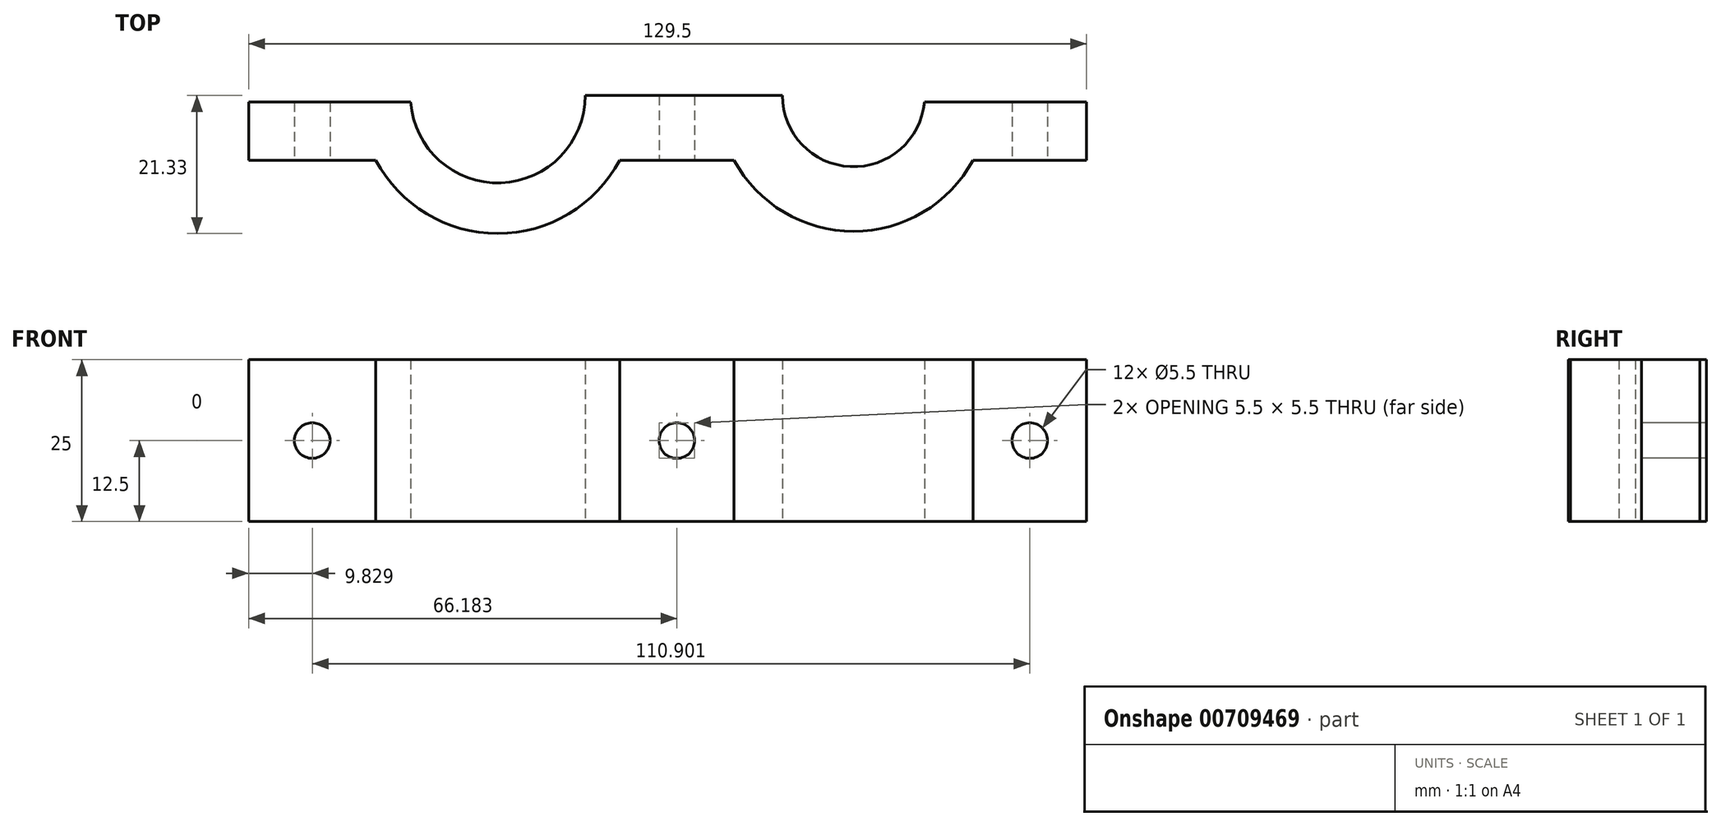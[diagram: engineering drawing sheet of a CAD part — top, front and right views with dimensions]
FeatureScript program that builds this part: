
annotation { "Feature Type Name" : "Feature", "Feature Type Description" : "" }
export const myFeature = defineFeature(function(context is Context, id is Id, definition is map)
    precondition{}
    {
        {
            var Q0;
            Q0=qCreatedBy(makeId("Top.planeOp"),FACE);
            var sketch = newSketch(context, id + "F0", { "sketchPlane" : qUnion([Q0])});
            skLineSegment(sketch, "E0", {"start": v(-63.41, -1.47) * mm, "end": v(-38.41, -1.47) * mm});
            skLineSegment(sketch, "E1", {"start": v(-11.41, -1.47) * mm, "end": v(19.09, -1.47) * mm});
            skLineSegment(sketch, "E2", {"start": v(41.09, -1.47) * mm, "end": v(66.09, -1.47) * mm});
            skLineSegment(sketch, "E3", {"start": v(66.09, -1.47) * mm, "end": v(66.09, -11.47) * mm});
            skLineSegment(sketch, "E4", {"start": v(66.09, -11.47) * mm, "end": v(48.55, -11.47) * mm});
            skLineSegment(sketch, "E5", {"start": v(-63.41, -1.47) * mm, "end": v(-63.41, -11.47) * mm});
            skLineSegment(sketch, "E6", {"start": v(-63.41, -11.47) * mm, "end": v(-43.75, -11.47) * mm});
            skArc(sketch, "E7", {"start": v(-38.41, -1.47) * mm, "mid": v(-24.91, -14.97) * mm, "end": v(-11.41, -1.47) * mm});
            skArc(sketch, "E8", {"start": v(19.09, -1.47) * mm, "mid": v(30.09, -12.47) * mm, "end": v(41.09, -1.47) * mm});
            skLineSegment(sketch, "E9", {"start": v(-6.08, -11.47) * mm, "end": v(11.62, -11.47) * mm});
            skArc(sketch, "E10", {"start": v(-43.75, -11.47) * mm, "mid": v(-24.91, -22.8) * mm, "end": v(-6.08, -11.47) * mm});
            skArc(sketch, "E11", {"start": v(11.62, -11.47) * mm, "mid": v(30.09, -22.47) * mm, "end": v(48.55, -11.47) * mm});
            skLineSegment(sketch, "E12", {"start": v(-24.91, -14.97) * mm, "end": v(-24.91, -22.8) * mm, "construction": true});
            skLineSegment(sketch, "E13", {"start": v(30.09, -12.47) * mm, "end": v(30.09, -22.47) * mm, "construction": true});
            skLineSegment(sketch, "E14", {"start": v(3.84, -1.47) * mm, "end": v(3.84, -11.47) * mm, "construction": true});
            skLineSegment(sketch, "E15", {"start": v(41.09, -1.47) * mm, "end": v(19.09, -1.47) * mm, "construction": true});
            skLineSegment(sketch, "E16", {"start": v(-11.41, -1.47) * mm, "end": v(-38.41, -1.47) * mm, "construction": true});
            skSolve(sketch);
        }
        {
            var Q0;
            Q0=makeQuery(id+"F0.imprint","IMPRINT",FACE,{"disambiguationData":[TD([[makeQuery(id+"F0.imprint","IMPRINT",EDGE,{"derivedFrom":sQuery(id+"F0.wireOp",EDGE,"E0")}),-1.0]])]});
            extrude(context, id + "F1", {"entities" : qUnion([Q0]), "depth" : 25 * mm, "offsetDistance" : 25 * mm});
        }
        {
            var Q0;
            Q0=makeQuery(id+"F1.opExtrude","SWEPT_FACE",FACE,{"disambiguationData":[OSD([sQuery(id+"F0.wireOp",EDGE,"E6")])]});
            var sketch = newSketch(context, id + "F2", { "sketchPlane" : qUnion([Q0])});
            skLineSegment(sketch, "E17", {"start": v(-53.58, 0) * mm, "end": v(-53.58, 25) * mm, "construction": true});
            skPoint(sketch, "E18", {"position": v(-53.58, 12.5) * mm});
            skSolve(sketch);
        }
        {
            var Q0;
            Q0=makeQuery(id+"F1.opExtrude","SWEPT_FACE",FACE,{"disambiguationData":[OSD([sQuery(id+"F0.wireOp",EDGE,"E4")])]});
            var sketch = newSketch(context, id + "F3", { "sketchPlane" : qUnion([Q0])});
            skLineSegment(sketch, "E19", {"start": v(57.32, 25) * mm, "end": v(57.32, 0) * mm, "construction": true});
            skPoint(sketch, "E20", {"position": v(57.32, 12.5) * mm});
            skSolve(sketch);
        }
        {
            var Q0;
            Q0=makeQuery(id+"F1.opExtrude","SWEPT_FACE",FACE,{"disambiguationData":[OSD([sQuery(id+"F0.wireOp",EDGE,"E9")])]});
            var sketch = newSketch(context, id + "F4", { "sketchPlane" : qUnion([Q0])});
            skLineSegment(sketch, "E21", {"start": v(2.77, 25) * mm, "end": v(2.77, 0) * mm, "construction": true});
            skPoint(sketch, "E22", {"position": v(2.77, 12.5) * mm});
            skSolve(sketch);
        }
        {
            var Q0;
            Q0=sQuery(id+"F2.wireOp",VERTEX,"E18");
            var Q1;
            Q1=sQuery(id+"F3.wireOp",VERTEX,"E20");
            var Q2;
            Q2=sQuery(id+"F4.wireOp",VERTEX,"E22");
            var Q3;
            Q3=makeQuery(id+"F1.opExtrude","SWEPT_BODY",BODY,{"disambiguationData":[OSD([sQuery(id+"F0.wireOp",EDGE,"E0"),sQuery(id+"F0.wireOp",EDGE,"E1"),sQuery(id+"F0.wireOp",EDGE,"E2"),sQuery(id+"F0.wireOp",EDGE,"E3"),sQuery(id+"F0.wireOp",EDGE,"E4"),sQuery(id+"F0.wireOp",EDGE,"E5"),sQuery(id+"F0.wireOp",EDGE,"E6"),sQuery(id+"F0.wireOp",EDGE,"E7"),sQuery(id+"F0.wireOp",EDGE,"E8"),sQuery(id+"F0.wireOp",EDGE,"E9"),sQuery(id+"F0.wireOp",EDGE,"E10"),sQuery(id+"F0.wireOp",EDGE,"E11")])]});
            hole(context, id + "F5", {"style" : HoleStyle.SIMPLE, "endStyle" : HoleEndStyle.BLIND, "standardTappedOrClearance" : lookupTablePath({ "standard" : "ISO", "fit" : "Normal", "size" : "M5", "type" : "Clearance" }), "standardBlindInLast" : lookupTablePath({ "fit" : "Standard", "standard" : "ISO", "size" : "M5", "type" : "Clearance" }), "holeDiameter" : 5.5 * mm, "majorDiameter" : 4 * mm, "holeDepth" : 14.1 * mm, "isTappedThrough" : true, "tappedDepth" : 12 * mm, "tapClearance" : 3, "locations" : qUnion([Q0, Q1, Q2]), "scope" : qUnion([Q3])});
        }
        {
            var Q0;
            Q0=makeQuery(id+"F1.opExtrude","SWEPT_FACE",FACE,{"disambiguationData":[OSD([sQuery(id+"F0.wireOp",EDGE,"E3")])]});
            var sketch = newSketch(context, id + "F6", { "sketchPlane" : qUnion([Q0])});
            skLineSegment(sketch, "E23.bottom", {"start": v(-1.47, 25) * mm, "end": v(-2.47, 25) * mm});
            skLineSegment(sketch, "E23.top", {"start": v(-1.47, 0) * mm, "end": v(-2.47, 0) * mm});
            skLineSegment(sketch, "E23.left", {"start": v(-1.47, 25) * mm, "end": v(-1.47, 0) * mm});
            skLineSegment(sketch, "E23.right", {"start": v(-2.47, 25) * mm, "end": v(-2.47, 0) * mm});
            skSolve(sketch);
        }
        {
            var Q0;
            Q0=makeQuery(id+"F6.imprint","IMPRINT",FACE,{"disambiguationData":[TD([[makeQuery(id+"F6.imprint","IMPRINT",EDGE,{"derivedFrom":sQuery(id+"F6.wireOp",EDGE,"E23.bottom")}),1.0]])]});
            extrude(context, id + "F7", {"entities" : qUnion([Q0]), "operationType" : NewBodyOperationType.REMOVE, "oppositeDirection" : true, "depth" : 30 * mm, "offsetDistance" : 25 * mm});
        }
        {
            var Q0;
            Q0=makeQuery(id+"F1.opExtrude","SWEPT_FACE",FACE,{"disambiguationData":[OSD([sQuery(id+"F0.wireOp",EDGE,"E5")])]});
            var sketch = newSketch(context, id + "F8", { "sketchPlane" : qUnion([Q0])});
            skLineSegment(sketch, "E24.bottom", {"start": v(1.47, 0) * mm, "end": v(2.47, 0) * mm});
            skLineSegment(sketch, "E24.top", {"start": v(1.47, 25) * mm, "end": v(2.47, 25) * mm});
            skLineSegment(sketch, "E24.left", {"start": v(1.47, 0) * mm, "end": v(1.47, 25) * mm});
            skLineSegment(sketch, "E24.right", {"start": v(2.47, 0) * mm, "end": v(2.47, 25) * mm});
            skSolve(sketch);
        }
        {
            var Q0;
            Q0 = qSketchRegion(id + "F8", true);
            extrude(context, id + "F9", {"entities" : qUnion([Q0]), "operationType" : NewBodyOperationType.REMOVE, "oppositeDirection" : true, "depth" : 30 * mm, "offsetDistance" : 25 * mm});
        }
    });
